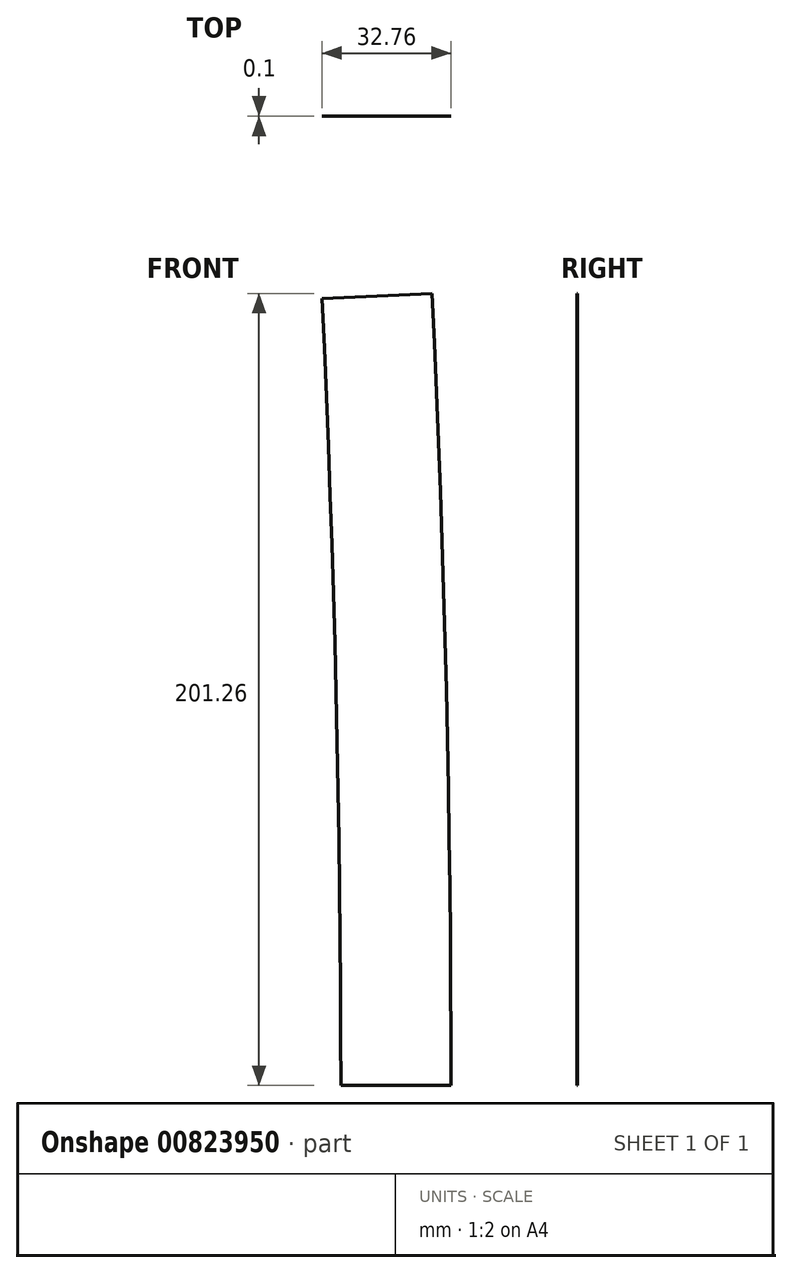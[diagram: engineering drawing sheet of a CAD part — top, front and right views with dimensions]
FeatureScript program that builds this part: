
annotation { "Feature Type Name" : "Feature", "Feature Type Description" : "" }
export const myFeature = defineFeature(function(context is Context, id is Id, definition is map)
    precondition{}
    {
        {
            var Q0;
            Q0=qCreatedBy(makeId("Front.planeOp"),FACE);
            var sketch = newSketch(context, id + "F0", { "sketchPlane" : qUnion([Q0])});
            skLineSegment(sketch, "E0", {"start": v(-28, 0) * mm, "end": v(0, 0) * mm});
            skLineSegment(sketch, "E1", {"start": v(-32.76, 199.92) * mm, "end": v(-4.8, 201.26) * mm});
            skArc(sketch, "E2", {"start": v(0, 0) * mm, "mid": v(-1.2, 100.66) * mm, "end": v(-4.8, 201.26) * mm});
            skArc(sketch, "E3", {"start": v(-28, 0) * mm, "mid": v(-29.2, 100) * mm, "end": v(-32.76, 199.92) * mm});
            skLineSegment(sketch, "E4", {"start": v(-4228.1, 0) * mm, "end": v(-4.8, 201.26) * mm, "construction": true});
            skSolve(sketch);
        }
        {
            var Q0;
            Q0=makeQuery(id+"F0.imprint","IMPRINT",FACE,{"disambiguationData":[TD([[makeQuery(id+"F0.imprint","IMPRINT",EDGE,{"derivedFrom":sQuery(id+"F0.wireOp",EDGE,"E0")}),1.0]])]});
            extrude(context, id + "F1", {"entities" : qUnion([Q0]), "depth" : 0.1 * mm, "offsetDistance" : 25 * mm});
        }
    });
